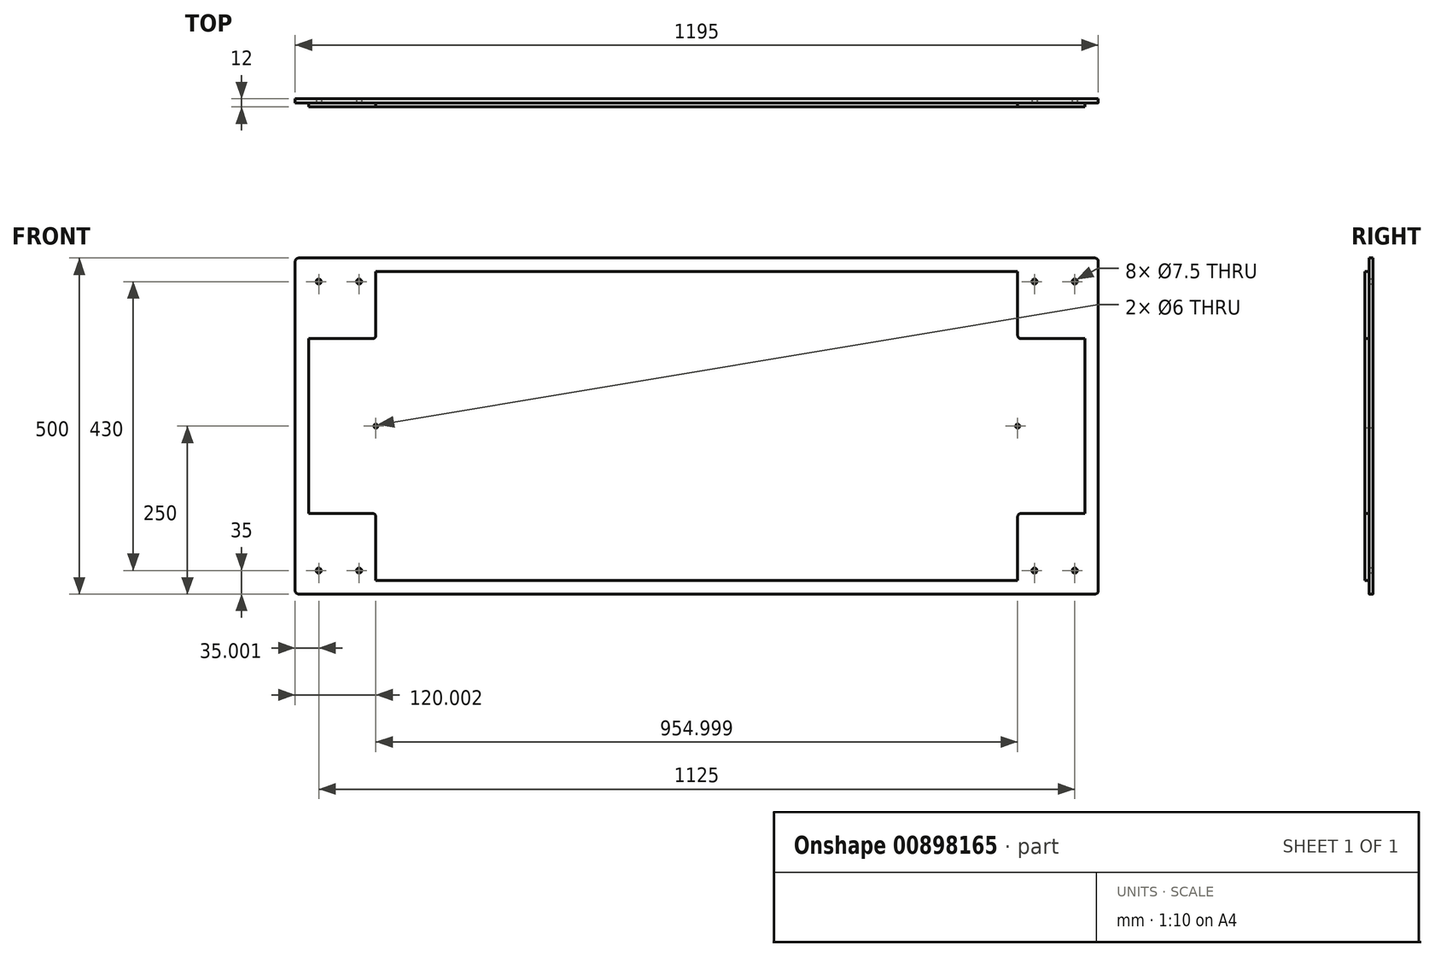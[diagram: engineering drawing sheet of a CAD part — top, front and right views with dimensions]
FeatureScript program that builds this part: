
annotation { "Feature Type Name" : "Feature", "Feature Type Description" : "" }
export const myFeature = defineFeature(function(context is Context, id is Id, definition is map)
    precondition{}
    {
        {
            var Q0;
            Q0=qCreatedBy(makeId("Front.planeOp"),FACE);
            var sketch = newSketch(context, id + "F0", { "sketchPlane" : qUnion([Q0])});
            skLineSegment(sketch, "E0.bottom", {"start": v(20, 286.06) * mm, "end": v(1175, 286.06) * mm});
            skLineSegment(sketch, "E0.top", {"start": v(20, -173.94) * mm, "end": v(1175, -173.94) * mm});
            skLineSegment(sketch, "E0.left", {"start": v(20, 286.06) * mm, "end": v(20, -173.94) * mm});
            skLineSegment(sketch, "E0.right", {"start": v(1175, 286.06) * mm, "end": v(1175, -173.94) * mm});
            skSolve(sketch);
        }
        {
            var Q0;
            Q0=qSketchRegion(id+"F0",true);
            extrude(context, id + "F1", {"entities" : qUnion([Q0]), "depth" : 6 * mm, "offsetDistance" : 25 * mm});
        }
        {
            var Q0;
            Q0=makeQuery(id+"F1.opExtrude","CAP_FACE",FACE,{"disambiguationData":[OSD([sQuery(id+"F0.wireOp",EDGE,"E0.bottom"),sQuery(id+"F0.wireOp",EDGE,"E0.top"),sQuery(id+"F0.wireOp",EDGE,"E0.left"),sQuery(id+"F0.wireOp",EDGE,"E0.right")])],"isStart":false});
            var sketch = newSketch(context, id + "F2", { "sketchPlane" : qUnion([Q0])});
            skLineSegment(sketch, "E1.bottom", {"start": v(20, 286.06) * mm, "end": v(120, 286.06) * mm});
            skLineSegment(sketch, "E1.top", {"start": v(20, 186.06) * mm, "end": v(120, 186.06) * mm});
            skLineSegment(sketch, "E1.left", {"start": v(20, 286.06) * mm, "end": v(20, 186.06) * mm});
            skLineSegment(sketch, "E1.right", {"start": v(120, 286.06) * mm, "end": v(120, 186.06) * mm});
            skLineSegment(sketch, "E2.bottom", {"start": v(1175, -173.94) * mm, "end": v(1075, -173.94) * mm});
            skLineSegment(sketch, "E2.top", {"start": v(1175, -73.94) * mm, "end": v(1075, -73.94) * mm});
            skLineSegment(sketch, "E2.left", {"start": v(1175, -173.94) * mm, "end": v(1175, -73.94) * mm});
            skLineSegment(sketch, "E2.right", {"start": v(1075, -173.94) * mm, "end": v(1075, -73.94) * mm});
            skLineSegment(sketch, "E3.bottom", {"start": v(1175, 286.06) * mm, "end": v(1075, 286.06) * mm});
            skLineSegment(sketch, "E3.top", {"start": v(1175, 186.06) * mm, "end": v(1075, 186.06) * mm});
            skLineSegment(sketch, "E3.left", {"start": v(1175, 286.06) * mm, "end": v(1175, 186.06) * mm});
            skLineSegment(sketch, "E3.right", {"start": v(1075, 286.06) * mm, "end": v(1075, 186.06) * mm});
            skLineSegment(sketch, "E4.bottom", {"start": v(20, -173.94) * mm, "end": v(120, -173.94) * mm});
            skLineSegment(sketch, "E4.top", {"start": v(20, -73.94) * mm, "end": v(120, -73.94) * mm});
            skLineSegment(sketch, "E4.left", {"start": v(20, -173.94) * mm, "end": v(20, -73.94) * mm});
            skLineSegment(sketch, "E4.right", {"start": v(120, -173.94) * mm, "end": v(120, -73.94) * mm});
            skSolve(sketch);
        }
        {
            var Q0;
            Q0=qSketchRegion(id+"F2",true);
            extrude(context, id + "F3", {"entities" : qUnion([Q0]), "operationType" : NewBodyOperationType.REMOVE, "oppositeDirection" : true, "depth" : 6 * mm, "offsetDistance" : 25 * mm});
        }
        {
            var Q0;
            Q0=makeQuery(id+"F3.boolean.opBoolean","COPY",EDGE,{"derivedFrom":makeQuery(id+"F3.opExtrude","SWEPT_EDGE",EDGE,{"disambiguationData":[OSD([sQuery(id+"F0.wireOp",EDGE,"E0.bottom"),sQuery(id+"F2.wireOp",EDGE,"E1.bottom"),sQuery(id+"F2.wireOp",EDGE,"E1.right")])]})});
            var Q1;
            Q1=makeQuery(id+"F3.boolean.opBoolean","COPY",EDGE,{"derivedFrom":makeQuery(id+"F3.opExtrude","SWEPT_EDGE",EDGE,{"disambiguationData":[OSD([sQuery(id+"F2.wireOp",EDGE,"E1.top"),sQuery(id+"F2.wireOp",EDGE,"E1.right")])]})});
            var Q2;
            Q2=makeQuery(id+"F3.boolean.opBoolean","COPY",EDGE,{"derivedFrom":makeQuery(id+"F3.opExtrude","SWEPT_EDGE",EDGE,{"disambiguationData":[OSD([sQuery(id+"F0.wireOp",EDGE,"E0.left"),sQuery(id+"F2.wireOp",EDGE,"E1.top"),sQuery(id+"F2.wireOp",EDGE,"E1.left")])]})});
            var Q3;
            Q3=makeQuery(id+"F3.boolean.opBoolean","COPY",EDGE,{"derivedFrom":makeQuery(id+"F3.opExtrude","SWEPT_EDGE",EDGE,{"disambiguationData":[OSD([sQuery(id+"F0.wireOp",EDGE,"E0.left"),sQuery(id+"F2.wireOp",EDGE,"E4.top"),sQuery(id+"F2.wireOp",EDGE,"E4.left")])]})});
            var Q4;
            Q4=makeQuery(id+"F3.boolean.opBoolean","COPY",EDGE,{"derivedFrom":makeQuery(id+"F3.opExtrude","SWEPT_EDGE",EDGE,{"disambiguationData":[OSD([sQuery(id+"F2.wireOp",EDGE,"E4.top"),sQuery(id+"F2.wireOp",EDGE,"E4.right")])]})});
            var Q5;
            Q5=makeQuery(id+"F3.boolean.opBoolean","COPY",EDGE,{"derivedFrom":makeQuery(id+"F3.opExtrude","SWEPT_EDGE",EDGE,{"disambiguationData":[OSD([sQuery(id+"F0.wireOp",EDGE,"E0.top"),sQuery(id+"F2.wireOp",EDGE,"E4.bottom"),sQuery(id+"F2.wireOp",EDGE,"E4.right")])]})});
            var Q6;
            Q6=makeQuery(id+"F3.boolean.opBoolean","COPY",EDGE,{"derivedFrom":makeQuery(id+"F3.opExtrude","SWEPT_EDGE",EDGE,{"disambiguationData":[OSD([sQuery(id+"F0.wireOp",EDGE,"E0.top"),sQuery(id+"F2.wireOp",EDGE,"E2.bottom"),sQuery(id+"F2.wireOp",EDGE,"E2.right")])]})});
            var Q7;
            Q7=makeQuery(id+"F3.boolean.opBoolean","COPY",EDGE,{"derivedFrom":makeQuery(id+"F3.opExtrude","SWEPT_EDGE",EDGE,{"disambiguationData":[OSD([sQuery(id+"F2.wireOp",EDGE,"E2.top"),sQuery(id+"F2.wireOp",EDGE,"E2.right")])]})});
            var Q8;
            Q8=makeQuery(id+"F3.boolean.opBoolean","COPY",EDGE,{"derivedFrom":makeQuery(id+"F3.opExtrude","SWEPT_EDGE",EDGE,{"disambiguationData":[OSD([sQuery(id+"F0.wireOp",EDGE,"E0.right"),sQuery(id+"F2.wireOp",EDGE,"E2.top"),sQuery(id+"F2.wireOp",EDGE,"E2.left")])]})});
            var Q9;
            Q9=makeQuery(id+"F3.boolean.opBoolean","COPY",EDGE,{"derivedFrom":makeQuery(id+"F3.opExtrude","SWEPT_EDGE",EDGE,{"disambiguationData":[OSD([sQuery(id+"F0.wireOp",EDGE,"E0.right"),sQuery(id+"F2.wireOp",EDGE,"E3.top"),sQuery(id+"F2.wireOp",EDGE,"E3.left")])]})});
            var Q10;
            Q10=makeQuery(id+"F3.boolean.opBoolean","COPY",EDGE,{"derivedFrom":makeQuery(id+"F3.opExtrude","SWEPT_EDGE",EDGE,{"disambiguationData":[OSD([sQuery(id+"F2.wireOp",EDGE,"E3.top"),sQuery(id+"F2.wireOp",EDGE,"E3.right")])]})});
            var Q11;
            Q11=makeQuery(id+"F3.boolean.opBoolean","COPY",EDGE,{"derivedFrom":makeQuery(id+"F3.opExtrude","SWEPT_EDGE",EDGE,{"disambiguationData":[OSD([sQuery(id+"F0.wireOp",EDGE,"E0.bottom"),sQuery(id+"F2.wireOp",EDGE,"E3.bottom"),sQuery(id+"F2.wireOp",EDGE,"E3.right")])]})});
            fillet(context, id + "F4", {"entities" : qUnion([Q0, Q1, Q2, Q3, Q4, Q5, Q6, Q7, Q8, Q9, Q10, Q11]), "radius" : 5 * mm, "tangentPropagation" : true, "allowEdgeOverflow" : false});
        }
        {
            var Q0;
            Q0=makeQuery(id+"F1.opExtrude","CAP_FACE",FACE,{"disambiguationData":[OSD([sQuery(id+"F0.wireOp",EDGE,"E0.bottom"),sQuery(id+"F0.wireOp",EDGE,"E0.top"),sQuery(id+"F0.wireOp",EDGE,"E0.left"),sQuery(id+"F0.wireOp",EDGE,"E0.right")])],"isStart":true});
            var sketch = newSketch(context, id + "F5", { "sketchPlane" : qUnion([Q0])});
            skLineSegment(sketch, "E5.bottom", {"start": v(-1195, 306.06) * mm, "end": v(0, 306.06) * mm});
            skLineSegment(sketch, "E5.top", {"start": v(-1195, -193.94) * mm, "end": v(0, -193.94) * mm});
            skLineSegment(sketch, "E5.left", {"start": v(-1195, 306.06) * mm, "end": v(-1195, -193.94) * mm});
            skLineSegment(sketch, "E5.right", {"start": v(0, 306.06) * mm, "end": v(0, -193.94) * mm});
            skLineSegment(sketch, "E6", {"start": v(-1175, 56.06) * mm, "end": v(284.96, 56.06) * mm, "construction": true});
            skLineSegment(sketch, "E7", {"start": v(-597.5, 286.06) * mm, "end": v(-597.5, -241.79) * mm, "construction": true});
            skPoint(sketch, "E8", {"position": v(-95, 271.06) * mm});
            skPoint(sketch, "E9", {"position": v(-35, 271.06) * mm});
            skPoint(sketch, "E10.MirrorP", {"position": v(-1100, 271.06) * mm});
            skPoint(sketch, "E11.MirrorP", {"position": v(-1160, 271.06) * mm});
            skPoint(sketch, "E12.MirrorP", {"position": v(-1100, -158.94) * mm});
            skPoint(sketch, "E13.MirrorP", {"position": v(-95, -158.94) * mm});
            skPoint(sketch, "E14.MirrorP", {"position": v(-1160, -158.94) * mm});
            skPoint(sketch, "E15.MirrorP", {"position": v(-35, -158.94) * mm});
            skSolve(sketch);
        }
        {
            var Q0;
            Q0 = qSketchRegion(id + "F5", true);
            extrude(context, id + "F6", {"entities" : qUnion([Q0]), "operationType" : NewBodyOperationType.ADD, "depth" : 3 * mm, "offsetDistance" : 25 * mm});
        }
        {
            var Q0;
            Q0=makeQuery(id+"F6.opExtrude","CAP_FACE",FACE,{"disambiguationData":[OSD([sQuery(id+"F5.wireOp",EDGE,"E5.bottom"),sQuery(id+"F5.wireOp",EDGE,"E5.top"),sQuery(id+"F5.wireOp",EDGE,"E5.left"),sQuery(id+"F5.wireOp",EDGE,"E5.right")])],"isStart":false});
            var sketch = newSketch(context, id + "F7", { "sketchPlane" : qUnion([Q0])});
            skLineSegment(sketch, "E16.bottom", {"start": v(0, -193.94) * mm, "end": v(-1195, -193.94) * mm});
            skLineSegment(sketch, "E16.top", {"start": v(0, 306.06) * mm, "end": v(-1195, 306.06) * mm});
            skLineSegment(sketch, "E16.left", {"start": v(0, -193.94) * mm, "end": v(0, 306.06) * mm});
            skLineSegment(sketch, "E16.right", {"start": v(-1195, -193.94) * mm, "end": v(-1195, 306.06) * mm});
            skSolve(sketch);
        }
        {
            var Q0;
            Q0 = qSketchRegion(id + "F7", true);
            extrude(context, id + "F8", {"entities" : qUnion([Q0]), "operationType" : NewBodyOperationType.ADD, "depth" : 3 * mm, "offsetDistance" : 25 * mm});
        }
        {
            var Q0;
            Q0=makeQuery(id+"F8.boolean.opBoolean","MERGE",EDGE,{"derivedFrom":[makeQuery(id+"F6.opExtrude","SWEPT_EDGE",EDGE,{"disambiguationData":[OSD([sQuery(id+"F5.wireOp",EDGE,"E5.bottom"),sQuery(id+"F5.wireOp",EDGE,"E5.right")])]}),makeQuery(id+"F8.opExtrude","SWEPT_EDGE",EDGE,{"disambiguationData":[OSD([sQuery(id+"F7.wireOp",EDGE,"E16.top"),sQuery(id+"F7.wireOp",EDGE,"E16.left")])]})]});
            var Q1;
            Q1=makeQuery(id+"F8.boolean.opBoolean","MERGE",EDGE,{"derivedFrom":[makeQuery(id+"F6.opExtrude","SWEPT_EDGE",EDGE,{"disambiguationData":[OSD([sQuery(id+"F5.wireOp",EDGE,"E5.top"),sQuery(id+"F5.wireOp",EDGE,"E5.right")])]}),makeQuery(id+"F8.opExtrude","SWEPT_EDGE",EDGE,{"disambiguationData":[OSD([sQuery(id+"F7.wireOp",EDGE,"E16.bottom"),sQuery(id+"F7.wireOp",EDGE,"E16.left")])]})]});
            var Q2;
            Q2=makeQuery(id+"F8.boolean.opBoolean","MERGE",EDGE,{"derivedFrom":[makeQuery(id+"F6.opExtrude","SWEPT_EDGE",EDGE,{"disambiguationData":[OSD([sQuery(id+"F5.wireOp",EDGE,"E5.top"),sQuery(id+"F5.wireOp",EDGE,"E5.left")])]}),makeQuery(id+"F8.opExtrude","SWEPT_EDGE",EDGE,{"disambiguationData":[OSD([sQuery(id+"F7.wireOp",EDGE,"E16.bottom"),sQuery(id+"F7.wireOp",EDGE,"E16.right")])]})]});
            var Q3;
            Q3=makeQuery(id+"F8.boolean.opBoolean","MERGE",EDGE,{"derivedFrom":[makeQuery(id+"F6.opExtrude","SWEPT_EDGE",EDGE,{"disambiguationData":[OSD([sQuery(id+"F5.wireOp",EDGE,"E5.bottom"),sQuery(id+"F5.wireOp",EDGE,"E5.left")])]}),makeQuery(id+"F8.opExtrude","SWEPT_EDGE",EDGE,{"disambiguationData":[OSD([sQuery(id+"F7.wireOp",EDGE,"E16.top"),sQuery(id+"F7.wireOp",EDGE,"E16.right")])]})]});
            fillet(context, id + "F9", {"entities" : qUnion([Q0, Q1, Q2, Q3]), "radius" : 5 * mm, "tangentPropagation" : true, "allowEdgeOverflow" : false});
        }
        {
            var Q0;
            Q0=sQuery(id+"F5.wireOp",VERTEX,"E9");
            var Q1;
            Q1=sQuery(id+"F5.wireOp",VERTEX,"E8");
            var Q2;
            Q2=sQuery(id+"F5.wireOp",VERTEX,"E15.MirrorP");
            var Q3;
            Q3=sQuery(id+"F5.wireOp",VERTEX,"E13.MirrorP");
            var Q4;
            Q4=sQuery(id+"F5.wireOp",VERTEX,"E10.MirrorP");
            var Q5;
            Q5=sQuery(id+"F5.wireOp",VERTEX,"E11.MirrorP");
            var Q6;
            Q6=sQuery(id+"F5.wireOp",VERTEX,"E14.MirrorP");
            var Q7;
            Q7=sQuery(id+"F5.wireOp",VERTEX,"E12.MirrorP");
            var Q8;
            Q8=makeQuery(id+"F1.opExtrude","SWEPT_BODY",BODY,{"disambiguationData":[OSD([sQuery(id+"F0.wireOp",EDGE,"E0.bottom"),sQuery(id+"F0.wireOp",EDGE,"E0.top"),sQuery(id+"F0.wireOp",EDGE,"E0.left"),sQuery(id+"F0.wireOp",EDGE,"E0.right")])]});
            hole(context, id + "F10", {"style" : HoleStyle.SIMPLE, "endStyle" : HoleEndStyle.THROUGH, "oppositeDirection" : true, "holeDiameter" : 7.5 * mm, "majorDiameter" : 5 * mm, "isTappedThrough" : true, "tappedDepth" : 12 * mm, "tapClearance" : 3, "startFromSketch" : true, "locations" : qUnion([Q0, Q1, Q2, Q3, Q4, Q5, Q6, Q7]), "scope" : qUnion([Q8])});
        }
        {
            var Q0;
            Q0=makeQuery(id+"F1.opExtrude","CAP_FACE",FACE,{"disambiguationData":[OSD([sQuery(id+"F0.wireOp",EDGE,"E0.bottom"),sQuery(id+"F0.wireOp",EDGE,"E0.top"),sQuery(id+"F0.wireOp",EDGE,"E0.left"),sQuery(id+"F0.wireOp",EDGE,"E0.right")])],"isStart":false});
            var sketch = newSketch(context, id + "F11", { "sketchPlane" : qUnion([Q0])});
            skPoint(sketch, "E17", {"position": v(120, 56.06) * mm});
            skPoint(sketch, "E18.MirrorP", {"position": v(1075, 56.06) * mm});
            skSolve(sketch);
        }
        {
            var Q0;
            Q0=sQuery(id+"F11.wireOp",VERTEX,"E17");
            var Q1;
            Q1=sQuery(id+"F11.wireOp",VERTEX,"E18.MirrorP");
            var Q2;
            Q2=makeQuery(id+"F1.opExtrude","SWEPT_BODY",BODY,{"disambiguationData":[OSD([sQuery(id+"F0.wireOp",EDGE,"E0.bottom"),sQuery(id+"F0.wireOp",EDGE,"E0.top"),sQuery(id+"F0.wireOp",EDGE,"E0.left"),sQuery(id+"F0.wireOp",EDGE,"E0.right")])]});
            hole(context, id + "F12", {"style" : HoleStyle.SIMPLE, "endStyle" : HoleEndStyle.THROUGH, "holeDiameter" : 6 * mm, "majorDiameter" : 5 * mm, "isTappedThrough" : true, "tappedDepth" : 12 * mm, "tapClearance" : 3, "startFromSketch" : true, "locations" : qUnion([Q0, Q1]), "scope" : qUnion([Q2])});
        }
    });
